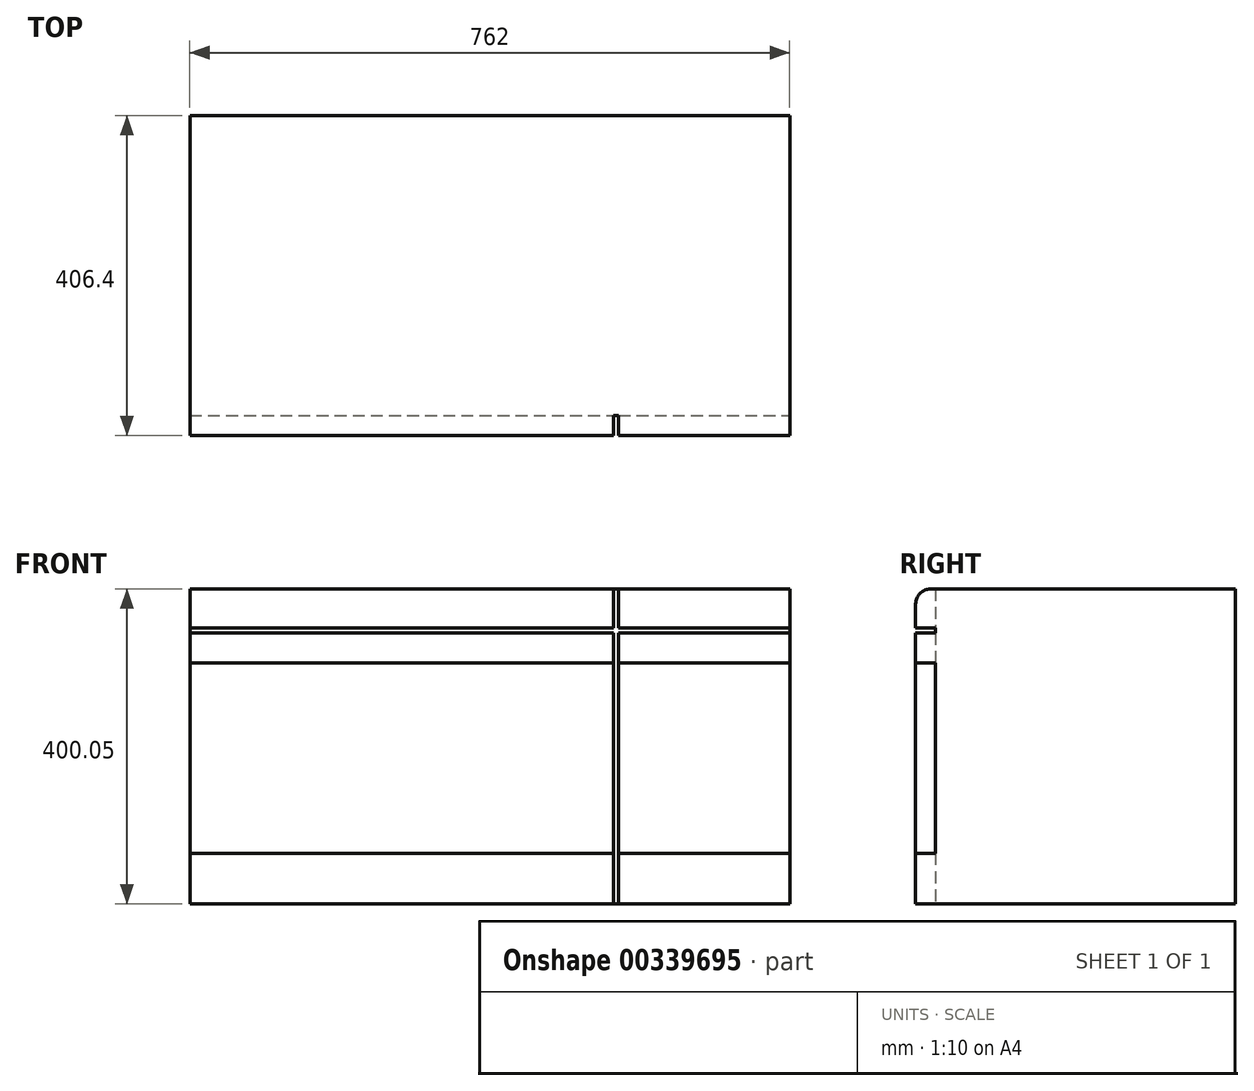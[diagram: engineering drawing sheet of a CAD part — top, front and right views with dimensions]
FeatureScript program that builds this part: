
annotation { "Feature Type Name" : "Feature", "Feature Type Description" : "" }
export const myFeature = defineFeature(function(context is Context, id is Id, definition is map)
    precondition{}
    {
        {
            var Q0;
            Q0=qCreatedBy(makeId("Front.planeOp"),FACE);
            var sketch = newSketch(context, id + "F0", { "sketchPlane" : qUnion([Q0])});
            skLineSegment(sketch, "E0.bottom", {"start": v(-837.7, 426.63) * mm, "end": v(-75.7, 426.63) * mm});
            skLineSegment(sketch, "E0.top", {"start": v(-837.7, 26.58) * mm, "end": v(-75.7, 26.58) * mm});
            skLineSegment(sketch, "E0.left", {"start": v(-837.7, 426.63) * mm, "end": v(-837.7, 26.58) * mm});
            skLineSegment(sketch, "E0.right", {"start": v(-75.7, 426.63) * mm, "end": v(-75.7, 26.58) * mm});
            skLineSegment(sketch, "E1", {"start": v(-837.7, 332.82) * mm, "end": v(-75.7, 332.82) * mm});
            skLineSegment(sketch, "E2", {"start": v(-837.7, 90.95) * mm, "end": v(-75.7, 90.95) * mm});
            skLineSegment(sketch, "E3", {"start": v(-837.7, 377.02) * mm, "end": v(-75.7, 377.02) * mm});
            skLineSegment(sketch, "E4", {"start": v(-293.1, 426.63) * mm, "end": v(-293.1, 26.58) * mm});
            skLineSegment(sketch, "E5.0", {"start": v(-837.7, 370.67) * mm, "end": v(-75.7, 370.67) * mm});
            skLineSegment(sketch, "E6.0", {"start": v(-299.45, 432.98) * mm, "end": v(-299.45, 26.58) * mm});
            skSolve(sketch);
        }
        {
            var Q0;
            Q0 = qSketchRegion(id + "F0", true);
            var Q1;
            {var subQ0=sQuery(id+"F0.wireOp",EDGE,"E6.0");var subQ1=sQuery(id+"F0.wireOp",EDGE,"E1");var subQ2=makeQuery(id+"F0.imprint","INTERSECT",VERTEX,{"derivedFrom":[subQ1,subQ0]});Q1=makeQuery(id+"F0.imprint","IMPRINT",FACE,{"disambiguationData":[TD([[makeQuery(id+"F0.imprint","IMPRINT",EDGE,{"disambiguationData":[TD([[subQ2,-1.0]])],"derivedFrom":subQ1}),1.0]])]});}
            var Q2;
            {var subQ0=sQuery(id+"F0.wireOp",EDGE,"E6.0");var subQ1=sQuery(id+"F0.wireOp",EDGE,"E3");var subQ2=makeQuery(id+"F0.imprint","INTERSECT",VERTEX,{"derivedFrom":[subQ1,subQ0]});Q2=makeQuery(id+"F0.imprint","IMPRINT",FACE,{"disambiguationData":[TD([[makeQuery(id+"F0.imprint","IMPRINT",EDGE,{"disambiguationData":[TD([[subQ2,-1.0]])],"derivedFrom":subQ1}),-1.0]])]});}
            var Q3;
            {var subQ0=sQuery(id+"F0.wireOp",EDGE,"E6.0");var subQ1=sQuery(id+"F0.wireOp",EDGE,"E1");var subQ2=makeQuery(id+"F0.imprint","INTERSECT",VERTEX,{"derivedFrom":[subQ1,subQ0]});Q3=makeQuery(id+"F0.imprint","IMPRINT",FACE,{"disambiguationData":[TD([[makeQuery(id+"F0.imprint","IMPRINT",EDGE,{"disambiguationData":[TD([[subQ2,-1.0]])],"derivedFrom":subQ1}),-1.0]])]});}
            extrude(context, id + "F1", {"entities" : qUnion([Q0, Q1, Q2, Q3]), "oppositeDirection" : true, "depth" : 406.4 * mm});
        }
        {
            var Q0;
            Q0=makeQuery(id+"F1.opExtrude","CAP_EDGE",EDGE,{"disambiguationData":[OSD([sQuery(id+"F0.wireOp",EDGE,"E0.bottom")])],"isStart":true});
            fillet(context, id + "F2", {"entities" : qUnion([Q0]), "radius" : 19.05 * mm, "tangentPropagation" : true, "allowEdgeOverflow" : false});
        }
        {
            var Q0;
            {var subQ0=sQuery(id+"F0.wireOp",EDGE,"E3");var subQ1=sQuery(id+"F0.wireOp",EDGE,"E0.left");var subQ2=makeQuery(id+"F0.imprint","INTERSECT",VERTEX,{"derivedFrom":[subQ1,subQ0]});Q0=makeQuery(id+"F0.imprint","IMPRINT",FACE,{"disambiguationData":[TD([[makeQuery(id+"F0.imprint","IMPRINT",EDGE,{"disambiguationData":[TD([[subQ2,-1.0]])],"derivedFrom":subQ1}),1.0]])]});}
            var Q1;
            {var subQ0=sQuery(id+"F0.wireOp",EDGE,"E4");var subQ1=sQuery(id+"F0.wireOp",EDGE,"E0.bottom");var subQ2=makeQuery(id+"F0.imprint","INTERSECT",VERTEX,{"derivedFrom":[subQ1,subQ0]});Q1=makeQuery(id+"F0.imprint","IMPRINT",FACE,{"disambiguationData":[TD([[makeQuery(id+"F0.imprint","IMPRINT",EDGE,{"disambiguationData":[TD([[subQ2,1.0]])],"derivedFrom":subQ1}),-1.0]])]});}
            var Q2;
            {var subQ0=sQuery(id+"F0.wireOp",EDGE,"E6.0");var subQ1=sQuery(id+"F0.wireOp",EDGE,"E3");var subQ2=makeQuery(id+"F0.imprint","INTERSECT",VERTEX,{"derivedFrom":[subQ1,subQ0]});Q2=makeQuery(id+"F0.imprint","IMPRINT",FACE,{"disambiguationData":[TD([[makeQuery(id+"F0.imprint","IMPRINT",EDGE,{"disambiguationData":[TD([[subQ2,-1.0]])],"derivedFrom":subQ1}),-1.0]])]});}
            var Q3;
            {var subQ0=sQuery(id+"F0.wireOp",EDGE,"E3");var subQ1=sQuery(id+"F0.wireOp",EDGE,"E0.right");var subQ2=makeQuery(id+"F0.imprint","INTERSECT",VERTEX,{"derivedFrom":[subQ1,subQ0]});Q3=makeQuery(id+"F0.imprint","IMPRINT",FACE,{"disambiguationData":[TD([[makeQuery(id+"F0.imprint","IMPRINT",EDGE,{"disambiguationData":[TD([[subQ2,-1.0]])],"derivedFrom":subQ1}),-1.0]])]});}
            var Q4;
            {var subQ0=sQuery(id+"F0.wireOp",EDGE,"E6.0");var subQ1=sQuery(id+"F0.wireOp",EDGE,"E1");var subQ2=makeQuery(id+"F0.imprint","INTERSECT",VERTEX,{"derivedFrom":[subQ1,subQ0]});Q4=makeQuery(id+"F0.imprint","IMPRINT",FACE,{"disambiguationData":[TD([[makeQuery(id+"F0.imprint","IMPRINT",EDGE,{"disambiguationData":[TD([[subQ2,-1.0]])],"derivedFrom":subQ1}),1.0]])]});}
            var Q5;
            {var subQ0=sQuery(id+"F0.wireOp",EDGE,"E6.0");var subQ1=sQuery(id+"F0.wireOp",EDGE,"E1");var subQ2=makeQuery(id+"F0.imprint","INTERSECT",VERTEX,{"derivedFrom":[subQ1,subQ0]});Q5=makeQuery(id+"F0.imprint","IMPRINT",FACE,{"disambiguationData":[TD([[makeQuery(id+"F0.imprint","IMPRINT",EDGE,{"disambiguationData":[TD([[subQ2,-1.0]])],"derivedFrom":subQ1}),-1.0]])]});}
            var Q6;
            {var subQ0=sQuery(id+"F0.wireOp",EDGE,"E4");var subQ1=sQuery(id+"F0.wireOp",EDGE,"E0.top");var subQ2=makeQuery(id+"F0.imprint","INTERSECT",VERTEX,{"derivedFrom":[subQ1,subQ0]});Q6=makeQuery(id+"F0.imprint","IMPRINT",FACE,{"disambiguationData":[TD([[makeQuery(id+"F0.imprint","IMPRINT",EDGE,{"disambiguationData":[TD([[subQ2,1.0]])],"derivedFrom":subQ1}),1.0]])]});}
            var Q7;
            {var subQ0=sQuery(id+"F0.wireOp",EDGE,"E1");var subQ1=sQuery(id+"F0.wireOp",EDGE,"E0.left");var subQ2=makeQuery(id+"F0.imprint","INTERSECT",VERTEX,{"derivedFrom":[subQ1,subQ0]});Q7=makeQuery(id+"F0.imprint","IMPRINT",FACE,{"disambiguationData":[TD([[makeQuery(id+"F0.imprint","IMPRINT",EDGE,{"disambiguationData":[TD([[subQ2,-1.0]])],"derivedFrom":subQ1}),1.0]])]});}
            var Q8;
            {var subQ0=sQuery(id+"F0.wireOp",EDGE,"E1");var subQ1=sQuery(id+"F0.wireOp",EDGE,"E0.right");var subQ2=makeQuery(id+"F0.imprint","INTERSECT",VERTEX,{"derivedFrom":[subQ1,subQ0]});Q8=makeQuery(id+"F0.imprint","IMPRINT",FACE,{"disambiguationData":[TD([[makeQuery(id+"F0.imprint","IMPRINT",EDGE,{"disambiguationData":[TD([[subQ2,-1.0]])],"derivedFrom":subQ1}),-1.0]])]});}
            extrude(context, id + "F3", {"entities" : qUnion([Q0, Q1, Q2, Q3, Q4, Q5, Q6, Q7, Q8]), "operationType" : NewBodyOperationType.REMOVE, "oppositeDirection" : true, "depth" : 25.4 * mm});
        }
        {
            var Q0;
            {var subQ0=sQuery(id+"F0.wireOp",EDGE,"E1");var subQ1=sQuery(id+"F0.wireOp",EDGE,"E0.left");var subQ2=makeQuery(id+"F0.imprint","INTERSECT",VERTEX,{"derivedFrom":[subQ1,subQ0]});Q0=makeQuery(id+"F0.imprint","IMPRINT",FACE,{"disambiguationData":[TD([[makeQuery(id+"F0.imprint","IMPRINT",EDGE,{"disambiguationData":[TD([[subQ2,-1.0]])],"derivedFrom":subQ1}),1.0]])]});}
            var Q1;
            {var subQ0=sQuery(id+"F0.wireOp",EDGE,"E1");var subQ1=sQuery(id+"F0.wireOp",EDGE,"E0.right");var subQ2=makeQuery(id+"F0.imprint","INTERSECT",VERTEX,{"derivedFrom":[subQ1,subQ0]});Q1=makeQuery(id+"F0.imprint","IMPRINT",FACE,{"disambiguationData":[TD([[makeQuery(id+"F0.imprint","IMPRINT",EDGE,{"disambiguationData":[TD([[subQ2,-1.0]])],"derivedFrom":subQ1}),-1.0]])]});}
            extrude(context, id + "F4", {"entities" : qUnion([Q0, Q1]), "oppositeDirection" : true, "depth" : 25.4 * mm});
        }
    });
